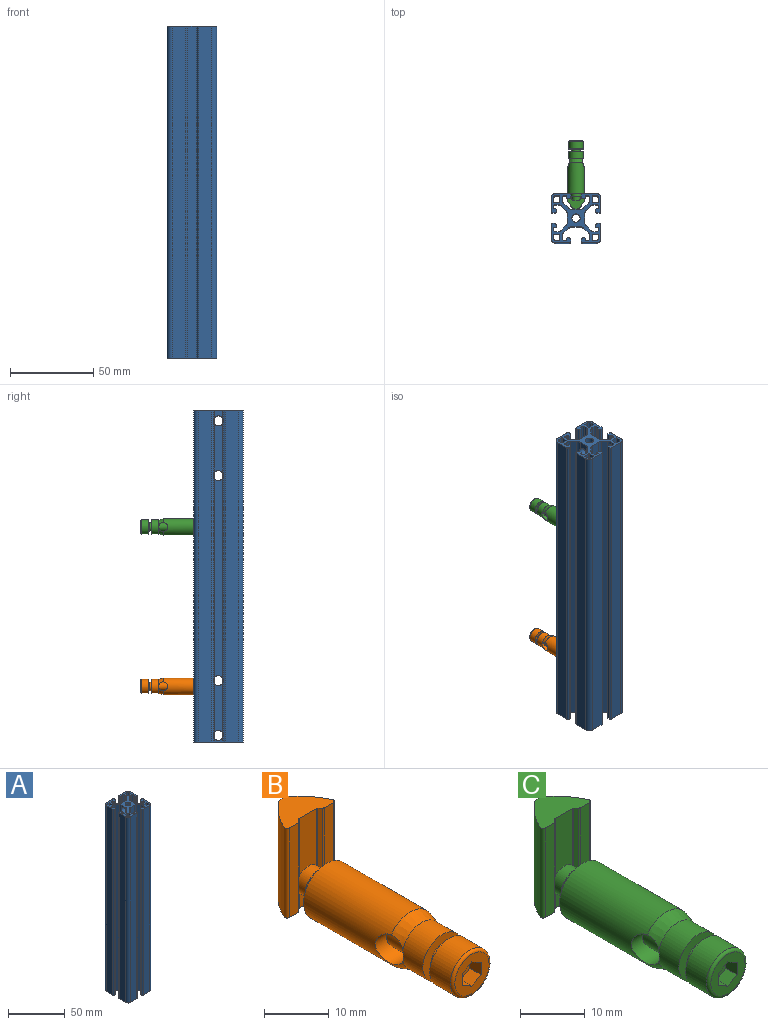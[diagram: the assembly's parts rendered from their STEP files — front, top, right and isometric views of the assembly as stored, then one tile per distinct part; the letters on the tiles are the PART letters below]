
ASSEMBLY  parts=3 mates=1
PART A: 179 faces, bbox 30x30x200 mm
  f0: cylinder r=2.5mm len=29.68mm, axis (0,0,1), area 443.7mm2, adj f5,f17
  f1: plane 29.98x5.19mm, normal (-1,0,0), area 144.5mm2, adj f5,f17,f20,f22
  f2: plane 29.98x5.19mm, normal (1,0,0), area 144.5mm2, adj f5,f17,f151,f153
  f3: plane 3.02x0.41mm, normal (-1,0,0), area 0.8mm2, adj f5,f153
  f4: plane 3.02x0.41mm, normal (-1,0,0), area 0.8mm2, adj f5,f151
  f5: cylinder r=3mm len=10.5mm, axis (1,0,0), area 153.8mm2, adj f0,f1,f2,f3,f4,f6,f7,f8
  f6: cylinder r=2.5mm len=120.18mm, axis (0,0,1), area 1865.2mm2, adj f5,f11
  f7: plane 120.48x5.19mm, normal (-1,0,0), area 613.9mm2, adj f5,f11,f20,f22
  f8: plane 120.48x5.19mm, normal (1,0,0), area 613.9mm2, adj f5,f11,f151,f153
  f9: plane 3.02x0.41mm, normal (-1,0,0), area 0.8mm2, adj f11,f153
  f10: plane 3.02x0.41mm, normal (-1,0,0), area 0.8mm2, adj f11,f151
  f11: cylinder r=3mm len=10.5mm, axis (1,0,0), area 153.8mm2, adj f6,f7,f8,f9,f10,f19,f20,f21
  f12: cylinder r=2.5mm len=5mm, axis (0,0,1), area 25.5mm2, adj f17,f175
  f13: plane 5.19x2.49mm, normal (-1,0,0), area 7.4mm2, adj f17,f20,f22,f175
  f14: plane 5.19x2.49mm, normal (1,0,0), area 7.4mm2, adj f17,f151,f153,f175
  f15: plane 3.02x0.41mm, normal (-1,0,0), area 0.8mm2, adj f17,f153
  f16: plane 3.02x0.41mm, normal (-1,0,0), area 0.8mm2, adj f17,f151
  f17: cylinder r=3mm len=10.5mm, axis (1,0,0), area 153.8mm2, adj f0,f1,f2,f12,f13,f14,f15,f16
  f18: cylinder r=2.5mm len=5mm, axis (0,0,1), area 64.7mm2, adj f83,f177
  f19: cylinder r=2.5mm len=29.68mm, axis (0,0,1), area 443.7mm2, adj f11,f177
  f20: cylinder r=3mm len=200mm, axis (0,0,1), area 467.9mm2, adj f1,f5,f7,f11,f13,f17,f21,f83
  f21: plane 29.98x5.19mm, normal (-1,0,0), area 144.5mm2, adj f11,f20,f22,f177
  f22: cylinder r=3mm len=200mm, axis (0,0,1), area 467.9mm2, adj f1,f5,f7,f11,f13,f17,f21,f83
  f23: plane 29.98x5.19mm, normal (1,0,0), area 144.5mm2, adj f11,f151,f153,f177
  f24: plane 200x2.05mm, normal (0,-1,0), area 410mm2, adj f25,f31,f83,f175
  f25: cylinder r=0.3mm len=200mm, axis (0,0,1), area 94.2mm2, adj f24,f26,f83,f175
  f26: plane 200x3.25mm, normal (-1,0,0), area 650mm2, adj f25,f27,f83,f175
  f27: cylinder r=0.3mm len=200mm, axis (0,0,1), area 94.2mm2, adj f26,f28,f83,f175
  f28: plane 200x3.25mm, normal (0,1,0), area 650mm2, adj f27,f29,f83,f175
  f29: cylinder r=0.3mm len=200mm, axis (0,0,1), area 94.2mm2, adj f28,f30,f83,f175
  f30: plane 200x2.05mm, normal (1,0,0), area 410mm2, adj f29,f31,f83,f175
  f31: cylinder r=1.5mm len=200mm, axis (0,0,1), area 471.2mm2, adj f24,f30,f83,f175
  f32: plane 200x2.05mm, normal (-1,0,0), area 410mm2, adj f33,f39,f83,f175
  f33: cylinder r=0.3mm len=200mm, axis (0,0,1), area 94.2mm2, adj f32,f34,f83,f175
  f34: plane 200x3.25mm, normal (0,1,0), area 650mm2, adj f33,f35,f83,f175
  f35: cylinder r=0.3mm len=200mm, axis (0,0,1), area 94.2mm2, adj f34,f36,f83,f175
  f36: plane 200x3.25mm, normal (1,0,0), area 650mm2, adj f35,f37,f83,f175
  f37: cylinder r=0.3mm len=200mm, axis (0,0,1), area 94.2mm2, adj f36,f38,f83,f175
  f38: plane 200x2.05mm, normal (0,-1,0), area 410mm2, adj f37,f39,f83,f175
  f39: cylinder r=1.5mm len=200mm, axis (0,0,1), area 471.2mm2, adj f32,f38,f83,f175
  f40: plane 200x2.05mm, normal (0,1,0), area 410mm2, adj f41,f47,f83,f175
  f41: cylinder r=0.3mm len=200mm, axis (0,0,1), area 94.2mm2, adj f40,f42,f83,f175
  f42: plane 200x3.25mm, normal (1,0,0), area 650mm2, adj f41,f43,f83,f175
  f43: cylinder r=0.3mm len=200mm, axis (0,0,1), area 94.2mm2, adj f42,f44,f83,f175
  f44: plane 200x3.25mm, normal (0,-1,0), area 650mm2, adj f43,f45,f83,f175
  f45: cylinder r=0.3mm len=200mm, axis (0,0,1), area 94.2mm2, adj f44,f46,f83,f175
  f46: plane 200x2.05mm, normal (-1,0,0), area 410mm2, adj f45,f47,f83,f175
  f47: cylinder r=1.5mm len=200mm, axis (0,0,1), area 471.2mm2, adj f40,f46,f83,f175
  f48: plane 200x2.05mm, normal (1,0,0), area 410mm2, adj f49,f55,f83,f175
  f49: cylinder r=0.3mm len=200mm, axis (0,0,1), area 94.2mm2, adj f48,f50,f83,f175
  f50: plane 200x3.25mm, normal (0,-1,0), area 650mm2, adj f49,f51,f83,f175
  f51: cylinder r=0.3mm len=200mm, axis (0,0,1), area 94.2mm2, adj f50,f52,f83,f175
  f52: plane 200x3.25mm, normal (-1,0,0), area 650mm2, adj f51,f53,f83,f175
  f53: cylinder r=0.3mm len=200mm, axis (0,0,1), area 94.2mm2, adj f52,f54,f83,f175
  f54: plane 200x2.05mm, normal (0,1,0), area 410mm2, adj f53,f55,f83,f175
  f55: cylinder r=1.5mm len=200mm, axis (0,0,1), area 471.2mm2, adj f48,f54,f83,f175
  f56: cylinder r=1mm len=200mm, axis (0,0,1), area 314.2mm2, adj f57,f83,f84,f175
  f57: plane 200x1.2mm, normal (1,0,0), area 240mm2, adj f56,f58,f83,f175
  f58: cylinder r=0.8mm len=200mm, axis (0,0,1), area 251.3mm2, adj f57,f59,f83,f175
  f59: plane 200x1.4mm, normal (0,1,0), area 280mm2, adj f58,f60,f83,f175
  f60: cylinder r=0.3mm len=200mm, axis (0,0,1), area 94.2mm2, adj f59,f61,f83,f175
  f61: plane 200x0.9mm, normal (-1,0,0), area 180mm2, adj f60,f62,f83,f175
  f62: cylinder r=0.3mm len=200mm, axis (0,0,1), area 94.2mm2, adj f61,f63,f83,f175
  f63: plane 200x1.25mm, normal (0,1,0), area 250mm2, adj f62,f64,f83,f175
  f64: cylinder r=1mm len=200mm, axis (0,0,1), area 314.2mm2, adj f63,f65,f83,f175
  f65: plane 200x1.69mm, normal (1,0,0), area 338.6mm2, adj f64,f66,f83,f175
  f66: cylinder r=3mm len=200mm, axis (0,0,1), area 471.2mm2, adj f65,f67,f83,f175
  f67: plane 200x2.56mm, normal (0.71,-0.71,0), area 723.2mm2, adj f66,f68,f83,f175
  f68: cylinder r=3mm len=200mm, axis (0,0,1), area 471.2mm2, adj f67,f69,f83,f175
  f69: plane 200x5.19mm, normal (0,-1,0), area 1037.3mm2, adj f68,f70,f83,f175
  f70: cylinder r=3mm len=200mm, axis (0,0,1), area 471.2mm2, adj f69,f71,f83,f175
  f71: plane 200x2.56mm, normal (-0.71,-0.71,0), area 723.2mm2, adj f70,f72,f83,f175
  f72: cylinder r=3mm len=200mm, axis (0,0,1), area 471.2mm2, adj f71,f73,f83,f175
  f73: plane 200x1.69mm, normal (-1,0,0), area 338.6mm2, adj f72,f74,f83,f175
  f74: cylinder r=1mm len=200mm, axis (0,0,1), area 314.2mm2, adj f73,f75,f83,f175
  f75: plane 200x1.25mm, normal (0,1,0), area 250mm2, adj f74,f76,f83,f175
  f76: cylinder r=0.3mm len=200mm, axis (0,0,1), area 94.2mm2, adj f75,f77,f83,f175
  f77: plane 200x0.9mm, normal (1,0,0), area 180mm2, adj f76,f78,f83,f175
  f78: cylinder r=0.3mm len=200mm, axis (0,0,1), area 94.2mm2, adj f77,f79,f83,f175
  f79: plane 200x1.4mm, normal (0,1,0), area 280mm2, adj f78,f80,f83,f175
  f80: cylinder r=0.8mm len=200mm, axis (0,0,1), area 251.3mm2, adj f79,f81,f83,f175
  f81: plane 200x1.2mm, normal (-1,0,0), area 240mm2, adj f80,f82,f83,f175
  f82: cylinder r=1mm len=200mm, axis (0,0,1), area 314.2mm2, adj f81,f83,f173,f175
  f83: plane 30x30mm, normal (0,0,-1), area 346.9mm2, adj f18,f20,f22,f24,f25,f26,f27,f28
  f84: plane 200x7.9mm, normal (0,-1,0), area 1580mm2, adj f56,f83,f174,f175
  f85: cylinder r=1mm len=200mm, axis (0,0,1), area 314.2mm2, adj f83,f86,f110,f175
  f86: plane 200x1.2mm, normal (0,-1,0), area 240mm2, adj f83,f85,f87,f175
  f87: cylinder r=0.8mm len=200mm, axis (0,0,1), area 251.3mm2, adj f83,f86,f88,f175
  f88: plane 200x1.4mm, normal (1,0,0), area 280mm2, adj f83,f87,f89,f175
  f89: cylinder r=0.3mm len=200mm, axis (0,0,1), area 94.2mm2, adj f83,f88,f90,f175
  f90: plane 200x0.9mm, normal (0,1,0), area 180mm2, adj f83,f89,f91,f175
  f91: cylinder r=0.3mm len=200mm, axis (0,0,1), area 94.2mm2, adj f83,f90,f92,f175
  f92: plane 200x1.25mm, normal (1,0,0), area 250mm2, adj f83,f91,f93,f175
  f93: cylinder r=1mm len=200mm, axis (0,0,1), area 314.2mm2, adj f83,f92,f94,f175
  f94: plane 200x1.69mm, normal (0,-1,0), area 338.6mm2, adj f83,f93,f95,f175
  f95: cylinder r=3mm len=200mm, axis (0,0,1), area 471.2mm2, adj f83,f94,f96,f175
  f96: plane 200x2.56mm, normal (-0.71,-0.71,0), area 723.2mm2, adj f20,f83,f95,f175
  f97: plane 5.19x4.99mm, normal (-1,0,0), area 20.4mm2, adj f20,f22,f83,f177
  f98: plane 200x2.56mm, normal (-0.71,0.71,0), area 723.2mm2, adj f22,f83,f99,f175
  f99: cylinder r=3mm len=200mm, axis (0,0,1), area 471.2mm2, adj f83,f98,f100,f175
  f100: plane 200x1.69mm, normal (0,1,0), area 338.6mm2, adj f83,f99,f101,f175
  f101: cylinder r=1mm len=200mm, axis (0,0,1), area 314.2mm2, adj f83,f100,f102,f175
  f102: plane 200x1.25mm, normal (1,0,0), area 250mm2, adj f83,f101,f103,f175
  f103: cylinder r=0.3mm len=200mm, axis (0,0,1), area 94.2mm2, adj f83,f102,f104,f175
  f104: plane 200x0.9mm, normal (0,-1,0), area 180mm2, adj f83,f103,f105,f175
  f105: cylinder r=0.3mm len=200mm, axis (0,0,1), area 94.2mm2, adj f83,f104,f106,f175
  f106: plane 200x1.4mm, normal (1,0,0), area 280mm2, adj f83,f105,f107,f175
  f107: cylinder r=0.8mm len=200mm, axis (0,0,1), area 251.3mm2, adj f83,f106,f108,f175
  f108: plane 200x1.2mm, normal (0,1,0), area 240mm2, adj f83,f107,f109,f175
  f109: cylinder r=1mm len=200mm, axis (0,0,1), area 314.2mm2, adj f83,f108,f167,f175
  f110: plane 200x7.9mm, normal (-1,0,0), area 1580mm2, adj f83,f85,f168,f175
  f111: cylinder r=1mm len=200mm, axis (0,0,1), area 314.2mm2, adj f83,f112,f138,f175
  f112: plane 200x1.2mm, normal (-1,0,0), area 240mm2, adj f83,f111,f113,f175
  f113: cylinder r=0.8mm len=200mm, axis (0,0,1), area 251.3mm2, adj f83,f112,f114,f175
  f114: plane 200x1.4mm, normal (0,-1,0), area 280mm2, adj f83,f113,f115,f175
  f115: cylinder r=0.3mm len=200mm, axis (0,0,1), area 94.2mm2, adj f83,f114,f116,f175
  f116: plane 200x0.9mm, normal (1,0,0), area 180mm2, adj f83,f115,f117,f175
  f117: cylinder r=0.3mm len=200mm, axis (0,0,1), area 94.2mm2, adj f83,f116,f118,f175
  f118: plane 200x1.25mm, normal (0,-1,0), area 250mm2, adj f83,f117,f119,f175
  f119: cylinder r=1mm len=200mm, axis (0,0,1), area 314.2mm2, adj f83,f118,f120,f175
  f120: plane 200x1.69mm, normal (-1,0,0), area 338.6mm2, adj f83,f119,f121,f175
  f121: cylinder r=3mm len=200mm, axis (0,0,1), area 471.2mm2, adj f83,f120,f122,f175
  f122: plane 200x2.56mm, normal (-0.71,0.71,0), area 723.2mm2, adj f83,f121,f123,f175
  f123: cylinder r=3mm len=200mm, axis (0,0,1), area 471.2mm2, adj f83,f122,f124,f175
  f124: plane 200x5.19mm, normal (0,1,0), area 1037.3mm2, adj f83,f123,f125,f175
  f125: cylinder r=3mm len=200mm, axis (0,0,1), area 471.2mm2, adj f83,f124,f126,f175
  f126: plane 200x2.56mm, normal (0.71,0.71,0), area 723.2mm2, adj f83,f125,f127,f175
  f127: cylinder r=3mm len=200mm, axis (0,0,1), area 471.2mm2, adj f83,f126,f128,f175
  f128: plane 200x1.69mm, normal (1,0,0), area 338.6mm2, adj f83,f127,f129,f175
  f129: cylinder r=1mm len=200mm, axis (0,0,1), area 314.2mm2, adj f83,f128,f130,f175
  f130: plane 200x1.25mm, normal (0,-1,0), area 250mm2, adj f83,f129,f131,f175
  f131: cylinder r=0.3mm len=200mm, axis (0,0,1), area 94.2mm2, adj f83,f130,f132,f175
  f132: plane 200x0.9mm, normal (-1,0,0), area 180mm2, adj f83,f131,f133,f175
  f133: cylinder r=0.3mm len=200mm, axis (0,0,1), area 94.2mm2, adj f83,f132,f134,f175
  f134: plane 200x1.4mm, normal (0,-1,0), area 280mm2, adj f83,f133,f135,f175
  f135: cylinder r=0.8mm len=200mm, axis (0,0,1), area 251.3mm2, adj f83,f134,f136,f175
  f136: plane 200x1.2mm, normal (1,0,0), area 240mm2, adj f83,f135,f137,f175
  f137: cylinder r=1mm len=200mm, axis (0,0,1), area 314.2mm2, adj f83,f136,f169,f175
  f138: plane 200x7.9mm, normal (0,1,0), area 1580mm2, adj f83,f111,f170,f175
  f139: cylinder r=1mm len=200mm, axis (0,0,1), area 314.2mm2, adj f83,f140,f166,f175
  f140: plane 200x1.2mm, normal (0,1,0), area 240mm2, adj f83,f139,f141,f175
  f141: cylinder r=0.8mm len=200mm, axis (0,0,1), area 251.3mm2, adj f83,f140,f142,f175
  f142: plane 200x1.4mm, normal (-1,0,0), area 280mm2, adj f83,f141,f143,f175
  f143: cylinder r=0.3mm len=200mm, axis (0,0,1), area 94.2mm2, adj f83,f142,f144,f175
  f144: plane 200x0.9mm, normal (0,-1,0), area 180mm2, adj f83,f143,f145,f175
  f145: cylinder r=0.3mm len=200mm, axis (0,0,1), area 94.2mm2, adj f83,f144,f146,f175
  f146: plane 200x1.25mm, normal (-1,0,0), area 250mm2, adj f83,f145,f147,f175
  f147: cylinder r=1mm len=200mm, axis (0,0,1), area 314.2mm2, adj f83,f146,f148,f175
  f148: plane 200x1.69mm, normal (0,1,0), area 338.6mm2, adj f83,f147,f149,f175
  f149: cylinder r=3mm len=200mm, axis (0,0,1), area 471.2mm2, adj f83,f148,f150,f175
  f150: plane 200x2.56mm, normal (0.71,0.71,0), area 723.2mm2, adj f83,f149,f151,f175
  f151: cylinder r=3mm len=200mm, axis (0,0,1), area 471.2mm2, adj f2,f4,f8,f10,f14,f16,f23,f83
  f152: plane 5.19x4.99mm, normal (1,0,0), area 20.4mm2, adj f83,f151,f153,f177
  f153: cylinder r=3mm len=200mm, axis (0,0,1), area 471.2mm2, adj f2,f3,f8,f9,f14,f15,f23,f83
  f154: plane 200x2.56mm, normal (0.71,-0.71,0), area 723.2mm2, adj f83,f153,f155,f175
  f155: cylinder r=3mm len=200mm, axis (0,0,1), area 471.2mm2, adj f83,f154,f156,f175
  f156: plane 200x1.69mm, normal (0,-1,0), area 338.6mm2, adj f83,f155,f157,f175
  f157: cylinder r=1mm len=200mm, axis (0,0,1), area 314.2mm2, adj f83,f156,f158,f175
  f158: plane 200x1.25mm, normal (-1,0,0), area 250mm2, adj f83,f157,f159,f175
  f159: cylinder r=0.3mm len=200mm, axis (0,0,1), area 94.2mm2, adj f83,f158,f160,f175
  f160: plane 200x0.9mm, normal (0,1,0), area 180mm2, adj f83,f159,f161,f175
  f161: cylinder r=0.3mm len=200mm, axis (0,0,1), area 94.2mm2, adj f83,f160,f162,f175
  f162: plane 200x1.4mm, normal (-1,0,0), area 280mm2, adj f83,f161,f163,f175
  f163: cylinder r=0.8mm len=200mm, axis (0,0,1), area 251.3mm2, adj f83,f162,f164,f175
  f164: plane 200x1.2mm, normal (0,-1,0), area 240mm2, adj f83,f163,f165,f175
  f165: cylinder r=1mm len=200mm, axis (0,0,1), area 314.2mm2, adj f83,f164,f171,f175
  f166: plane 200x7.9mm, normal (1,0,0), area 1580mm2, adj f83,f139,f172,f175
  f167: plane 200x7.9mm, normal (-1,0,0), area 1580mm2, adj f83,f109,f174,f175
  f168: cylinder r=3mm len=200mm, axis (0,0,1), area 942.5mm2, adj f83,f110,f169,f175
  f169: plane 200x7.9mm, normal (0,1,0), area 1580mm2, adj f83,f137,f168,f175
  f170: cylinder r=3mm len=200mm, axis (0,0,1), area 942.5mm2, adj f83,f138,f171,f175
  f171: plane 200x7.9mm, normal (1,0,0), area 1580mm2, adj f83,f165,f170,f175
  f172: cylinder r=3mm len=200mm, axis (0,0,1), area 942.5mm2, adj f83,f166,f173,f175
  f173: plane 200x7.9mm, normal (0,-1,0), area 1580mm2, adj f82,f83,f172,f175
  f174: cylinder r=3mm len=200mm, axis (0,0,1), area 942.5mm2, adj f83,f84,f167,f175
  f175: plane 30x30mm, normal (0,0,1), area 346.9mm2, adj f12,f13,f14,f20,f22,f24,f25,f26
  f176: plane 3.02x0.41mm, normal (-1,0,0), area 0.8mm2, adj f153,f177
  f177: cylinder r=3mm len=10.5mm, axis (1,0,0), area 153.8mm2, adj f18,f19,f20,f21,f22,f23,f97,f152
  f178: plane 3.02x0.41mm, normal (-1,0,0), area 0.8mm2, adj f151,f177
PART B: 49 faces, bbox 10.6x41.6x17.5 mm
  f0: cone r=4.62mm half-angle=16.7deg, axis (0,1,0), area 25.7mm2, adj f1,f4,f5
  f1: cylinder r=4.25mm len=8.5mm, axis (0,-1,0), area 120.2mm2, adj f0,f3,f5,f47
  f2: cylinder r=3.06mm len=6.11mm, axis (0,-1,0), area 30.7mm2, adj f46,f48
  f3: cone r=4.62mm half-angle=16.7deg, axis (0,1,0), area 25.7mm2, adj f1,f4,f5
  f4: cylinder r=5mm len=18.4mm, axis (0,-1,0), area 554.2mm2, adj f0,f3,f5,f48
  f5: cylinder r=2.7mm len=10mm, axis (1,0,0), area 102.4mm2, adj f0,f1,f3,f4,f11
  f6: cylinder r=2.5mm len=5mm, axis (0,-1,0), area 19mm2, adj f10,f24,f25,f26,f35,f36,f37
  f7: cylinder r=4.25mm len=8.5mm, axis (0,1,0), area 120.2mm2, adj f8,f23
  f8: torus R=3.75mm, axis (0,1,0), area 20.1mm2, adj f7,f20
  f9: torus R=2.7mm, axis (0,1,0), area 5.1mm2, adj f13,f23
  f10: cone r=1.25mm half-angle=45deg, axis (0,-1,0), area 9.8mm2, adj f6,f14
  f11: cylinder r=2.5mm len=5.4mm, axis (0,1,0), area 61.4mm2, adj f5
  f12: cylinder r=2.5mm len=5mm, axis (0,1,0), area 35.5mm2, adj f27,f28,f29,f30,f31,f41,f42,f43
  f13: cylinder r=2.5mm len=5mm, axis (0,1,0), area 20.4mm2, adj f9,f47
  f14: plane 4.02x4.02mm, normal (0,1,0), area 12.7mm2, adj f10
  f15: plane 2.5x2mm, normal (-0.5,0,0.87), area 5.8mm2, adj f17,f19,f20,f22
  f16: plane 2.5x2mm, normal (0.5,0,-0.87), area 5.8mm2, adj f17,f18,f20,f21
  f17: plane 4.62x4mm, normal (0,-1,0), area 13.9mm2, adj f15,f16,f18,f19,f21,f22
  f18: plane 2.5x2mm, normal (-0.5,0,-0.87), area 5.8mm2, adj f16,f17,f20,f22
  f19: plane 2.5x2mm, normal (0.5,0,0.87), area 5.8mm2, adj f15,f17,f20,f21
  f20: plane 7.5x7.5mm, normal (0,-1,0), area 30.3mm2, adj f8,f15,f16,f18,f19,f21,f22
  f21: plane 2.5x2.31mm, normal (1,0,0), area 5.8mm2, adj f16,f17,f19,f20
  f22: plane 2.5x2.31mm, normal (-1,0,0), area 5.8mm2, adj f15,f17,f18,f20
  f23: plane 8.5x8.5mm, normal (0,1,0), area 33.8mm2, adj f7,f9
  f24: cylinder r=15.37mm len=17mm, axis (0,0,-1), area 105.9mm2, adj f6,f25,f37,f38,f44,f45
  f25: cylinder r=2mm len=2.4mm, axis (0,0,-1), area 3.3mm2, adj f6,f24,f26,f44
  f26: cylinder r=2mm len=2.4mm, axis (0,0,-1), area 3.3mm2, adj f6,f25,f35,f44
  f27: plane 17x0.53mm, normal (-0.71,-0.71,0), area 11.6mm2, adj f12,f28,f31,f32,f44,f45
  f28: cylinder r=0.3mm len=3.12mm, axis (0,0,-1), area 0.7mm2, adj f12,f27,f29,f44
  f29: plane 3.75x2.85mm, normal (0,-1,0), area 8.5mm2, adj f12,f28,f30,f44
  f30: cylinder r=0.3mm len=3.12mm, axis (0,0,-1), area 0.7mm2, adj f12,f29,f41,f44
  f31: cylinder r=0.3mm len=11.12mm, axis (0,0,-1), area 2.6mm2, adj f12,f27,f43,f45
  f32: cylinder r=0.3mm len=17mm, axis (0,0,-1), area 4mm2, adj f27,f33,f44,f45
  f33: plane 17x1.98mm, normal (0,-1,0), area 33.6mm2, adj f32,f34,f44,f45
  f34: cylinder r=0.5mm len=17mm, axis (0,0,-1), area 17.2mm2, adj f33,f35,f44,f45
  f35: cylinder r=15.37mm len=17mm, axis (0,0,-1), area 106mm2, adj f6,f26,f34,f36,f44,f45
  f36: cylinder r=2mm len=10.4mm, axis (0,0,-1), area 15.2mm2, adj f6,f35,f37,f45
  f37: cylinder r=2mm len=10.4mm, axis (0,0,-1), area 15.2mm2, adj f6,f24,f36,f45
  f38: cylinder r=0.5mm len=17mm, axis (0,0,-1), area 17.2mm2, adj f24,f39,f44,f45
  f39: plane 17x1.98mm, normal (0,-1,0), area 33.6mm2, adj f38,f40,f44,f45
  f40: cylinder r=0.3mm len=17mm, axis (0,0,-1), area 4mm2, adj f39,f41,f44,f45
  f41: plane 17x0.53mm, normal (0.71,-0.71,0), area 11.6mm2, adj f12,f30,f40,f42,f44,f45
  f42: cylinder r=0.3mm len=11.12mm, axis (0,0,-1), area 2.6mm2, adj f12,f41,f43,f45
  f43: plane 10.85x3.75mm, normal (0,-1,0), area 38.5mm2, adj f12,f31,f42,f45
  f44: plane 10.6x6.4mm, normal (0,0,-1), area 42.2mm2, adj f24,f25,f26,f27,f28,f29,f30,f32
  f45: plane 10.6x6.4mm, normal (0,0,1), area 42.2mm2, adj f24,f27,f31,f32,f33,f34,f35,f36
  f46: plane 6.11x6.11mm, normal (0,1,0), area 9.7mm2, adj f2,f12
  f47: plane 8.5x8.5mm, normal (0,-1,0), area 37.1mm2, adj f1,f13
  f48: plane 10x10mm, normal (0,1,0), area 49.2mm2, adj f2,f4
PART C: 49 faces, bbox 10.6x41.6x17.5 mm
  f0: cone r=4.62mm half-angle=16.7deg, axis (0,1,0), area 25.7mm2, adj f1,f4,f5
  f1: cylinder r=4.25mm len=8.5mm, axis (0,-1,0), area 120.2mm2, adj f0,f3,f5,f47
  f2: cylinder r=3.06mm len=6.11mm, axis (0,-1,0), area 30.7mm2, adj f46,f48
  f3: cone r=4.62mm half-angle=16.7deg, axis (0,1,0), area 25.7mm2, adj f1,f4,f5
  f4: cylinder r=5mm len=18.4mm, axis (0,-1,0), area 554.2mm2, adj f0,f3,f5,f48
  f5: cylinder r=2.7mm len=10mm, axis (1,0,0), area 102.4mm2, adj f0,f1,f3,f4,f11
  f6: cylinder r=2.5mm len=5mm, axis (0,-1,0), area 19mm2, adj f10,f24,f25,f26,f35,f36,f37
  f7: cylinder r=4.25mm len=8.5mm, axis (0,1,0), area 120.2mm2, adj f8,f23
  f8: torus R=3.75mm, axis (0,1,0), area 20.1mm2, adj f7,f20
  f9: torus R=2.7mm, axis (0,1,0), area 5.1mm2, adj f13,f23
  f10: cone r=1.25mm half-angle=45deg, axis (0,-1,0), area 9.8mm2, adj f6,f14
  f11: cylinder r=2.5mm len=5.4mm, axis (0,1,0), area 61.4mm2, adj f5
  f12: cylinder r=2.5mm len=5mm, axis (0,1,0), area 35.5mm2, adj f27,f28,f29,f30,f31,f41,f42,f43
  f13: cylinder r=2.5mm len=5mm, axis (0,1,0), area 20.4mm2, adj f9,f47
  f14: plane 4.02x4.02mm, normal (0,1,0), area 12.7mm2, adj f10
  f15: plane 2.5x2mm, normal (-0.5,0,0.87), area 5.8mm2, adj f17,f19,f20,f22
  f16: plane 2.5x2mm, normal (0.5,0,-0.87), area 5.8mm2, adj f17,f18,f20,f21
  f17: plane 4.62x4mm, normal (0,-1,0), area 13.9mm2, adj f15,f16,f18,f19,f21,f22
  f18: plane 2.5x2mm, normal (-0.5,0,-0.87), area 5.8mm2, adj f16,f17,f20,f22
  f19: plane 2.5x2mm, normal (0.5,0,0.87), area 5.8mm2, adj f15,f17,f20,f21
  f20: plane 7.5x7.5mm, normal (0,-1,0), area 30.3mm2, adj f8,f15,f16,f18,f19,f21,f22
  f21: plane 2.5x2.31mm, normal (1,0,0), area 5.8mm2, adj f16,f17,f19,f20
  f22: plane 2.5x2.31mm, normal (-1,0,0), area 5.8mm2, adj f15,f17,f18,f20
  f23: plane 8.5x8.5mm, normal (0,1,0), area 33.8mm2, adj f7,f9
  f24: cylinder r=15.37mm len=17mm, axis (0,0,-1), area 105.9mm2, adj f6,f25,f37,f38,f44,f45
  f25: cylinder r=2mm len=2.4mm, axis (0,0,-1), area 3.3mm2, adj f6,f24,f26,f44
  f26: cylinder r=2mm len=2.4mm, axis (0,0,-1), area 3.3mm2, adj f6,f25,f35,f44
  f27: plane 17x0.53mm, normal (-0.71,-0.71,0), area 11.6mm2, adj f12,f28,f31,f32,f44,f45
  f28: cylinder r=0.3mm len=3.12mm, axis (0,0,-1), area 0.7mm2, adj f12,f27,f29,f44
  f29: plane 3.75x2.85mm, normal (0,-1,0), area 8.5mm2, adj f12,f28,f30,f44
  f30: cylinder r=0.3mm len=3.12mm, axis (0,0,-1), area 0.7mm2, adj f12,f29,f41,f44
  f31: cylinder r=0.3mm len=11.12mm, axis (0,0,-1), area 2.6mm2, adj f12,f27,f43,f45
  f32: cylinder r=0.3mm len=17mm, axis (0,0,-1), area 4mm2, adj f27,f33,f44,f45
  f33: plane 17x1.98mm, normal (0,-1,0), area 33.6mm2, adj f32,f34,f44,f45
  f34: cylinder r=0.5mm len=17mm, axis (0,0,-1), area 17.2mm2, adj f33,f35,f44,f45
  f35: cylinder r=15.37mm len=17mm, axis (0,0,-1), area 106mm2, adj f6,f26,f34,f36,f44,f45
  f36: cylinder r=2mm len=10.4mm, axis (0,0,-1), area 15.2mm2, adj f6,f35,f37,f45
  f37: cylinder r=2mm len=10.4mm, axis (0,0,-1), area 15.2mm2, adj f6,f24,f36,f45
  f38: cylinder r=0.5mm len=17mm, axis (0,0,-1), area 17.2mm2, adj f24,f39,f44,f45
  f39: plane 17x1.98mm, normal (0,-1,0), area 33.6mm2, adj f38,f40,f44,f45
  f40: cylinder r=0.3mm len=17mm, axis (0,0,-1), area 4mm2, adj f39,f41,f44,f45
  f41: plane 17x0.53mm, normal (0.71,-0.71,0), area 11.6mm2, adj f12,f30,f40,f42,f44,f45
  f42: cylinder r=0.3mm len=11.12mm, axis (0,0,-1), area 2.6mm2, adj f12,f41,f43,f45
  f43: plane 10.85x3.75mm, normal (0,-1,0), area 38.5mm2, adj f12,f31,f42,f45
  f44: plane 10.6x6.4mm, normal (0,0,-1), area 42.2mm2, adj f24,f25,f26,f27,f28,f29,f30,f32
  f45: plane 10.6x6.4mm, normal (0,0,1), area 42.2mm2, adj f24,f27,f31,f32,f33,f34,f35,f36
  f46: plane 6.11x6.11mm, normal (0,1,0), area 9.7mm2, adj f2,f12
  f47: plane 8.5x8.5mm, normal (0,-1,0), area 37.1mm2, adj f1,f13
  f48: plane 10x10mm, normal (0,1,0), area 49.2mm2, adj f2,f4
PLACE A rot(axis=(1,0,0),180deg) t=(12,-100,-185)mm
PLACE B rot(axis=(0,0,1),180deg) t=(12,-100.05,-163.5)mm
PLACE C rot(axis=(0,0,1),180deg) t=(12,-100.05,70)mm
MATE slider B.f45 <-> A.f175  axis (0,0,1) through (12,20.25,-154)mm
